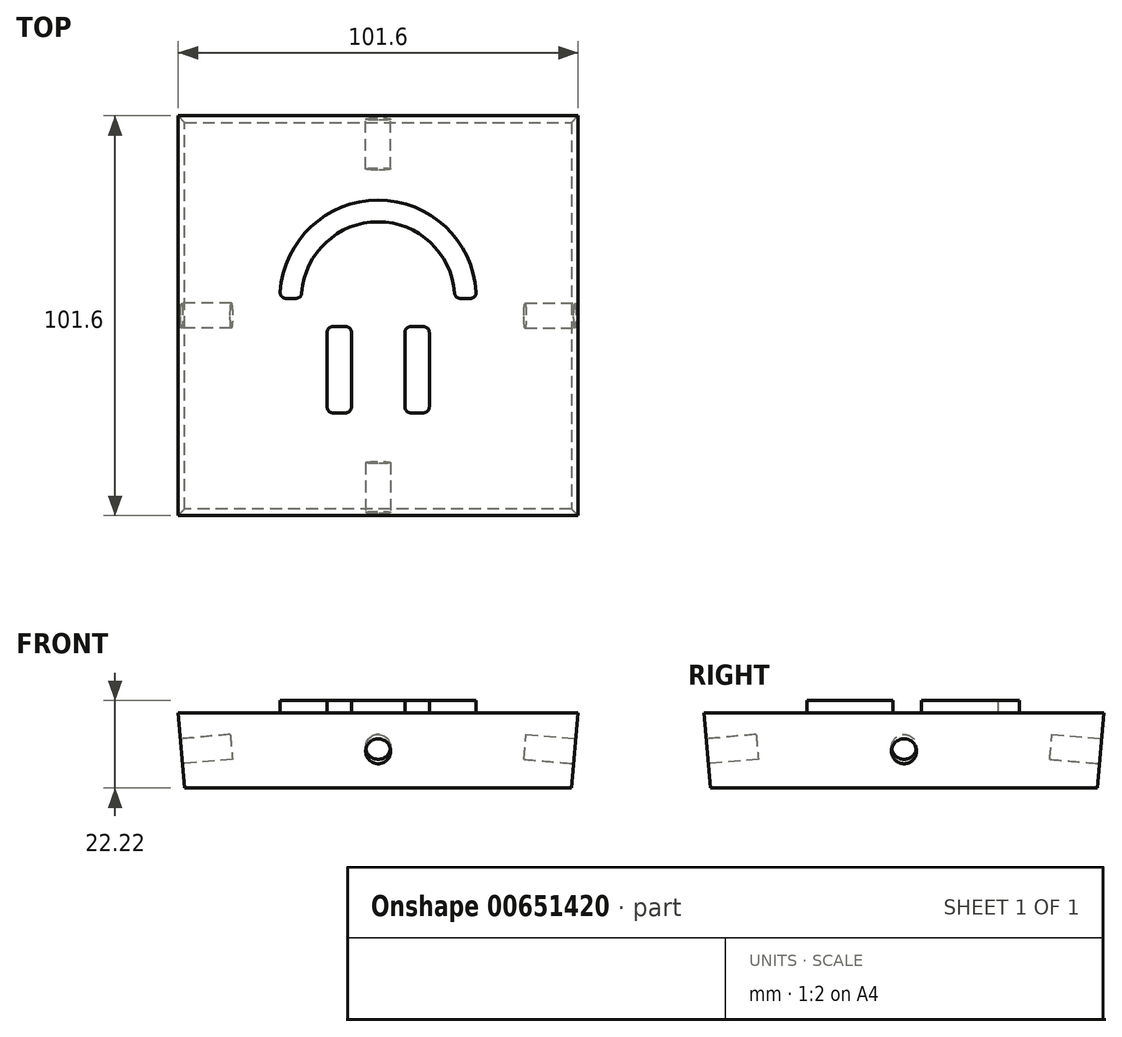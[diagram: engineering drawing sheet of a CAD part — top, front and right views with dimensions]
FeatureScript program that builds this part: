
annotation { "Feature Type Name" : "Feature", "Feature Type Description" : "" }
export const myFeature = defineFeature(function(context is Context, id is Id, definition is map)
    precondition{}
    {
        {
            var Q0;
            Q0=qCreatedBy(makeId("Top.planeOp"),FACE);
            var sketch = newSketch(context, id + "F0", { "sketchPlane" : qUnion([Q0])});
            skLineSegment(sketch, "E0.bottom", {"start": v(-50.8, 50.8) * mm, "end": v(50.8, 50.8) * mm});
            skLineSegment(sketch, "E0.top", {"start": v(-50.8, -50.8) * mm, "end": v(50.8, -50.8) * mm});
            skLineSegment(sketch, "E0.left", {"start": v(-50.8, 50.8) * mm, "end": v(-50.8, -50.8) * mm});
            skLineSegment(sketch, "E0.right", {"start": v(50.8, 50.8) * mm, "end": v(50.8, -50.8) * mm});
            skPoint(sketch, "E0.middle", {"position": v(0, 0) * mm});
            skSolve(sketch);
        }
        {
            var Q0;
            Q0=makeQuery(id+"F0.imprint","IMPRINT",FACE,{"disambiguationData":[TD([[makeQuery(id+"F0.imprint","IMPRINT",EDGE,{"derivedFrom":sQuery(id+"F0.wireOp",EDGE,"E0.bottom")}),-1.0]])]});
            extrude(context, id + "F1", {"entities" : qUnion([Q0]), "depth" : 19.05 * mm, "offsetDistance" : 25.4 * mm});
        }
        {
            var Q0;
            Q0=makeQuery(id+"F1.opExtrude","CAP_EDGE",EDGE,{"disambiguationData":[OSD([sQuery(id+"F0.wireOp",EDGE,"E0.right")])],"isStart":false});
            var Q1;
            Q1=makeQuery(id+"F1.opExtrude","CAP_EDGE",EDGE,{"disambiguationData":[OSD([sQuery(id+"F0.wireOp",EDGE,"E0.top")])],"isStart":false});
            var Q2;
            Q2=makeQuery(id+"F1.opExtrude","CAP_EDGE",EDGE,{"disambiguationData":[OSD([sQuery(id+"F0.wireOp",EDGE,"E0.left")])],"isStart":false});
            var Q3;
            Q3=makeQuery(id+"F1.opExtrude","CAP_EDGE",EDGE,{"disambiguationData":[OSD([sQuery(id+"F0.wireOp",EDGE,"E0.bottom")])],"isStart":false});
            chamfer(context, id + "F2", {"entities" : qUnion([Q0, Q1, Q2, Q3]), "chamferType" : ChamferType.OFFSET_ANGLE, "width" : 19.05 * mm, "oppositeDirection" : false, "angle" : 5 * degree, "tangentPropagation" : true});
        }
        {
            var Q0;
            Q0=makeQuery(id+"F2.opChamfer","BLEND_FACE",FACE,{"disambiguationData":[OSD([sQuery(id+"F0.wireOp",EDGE,"E0.bottom")])]});
            var sketch = newSketch(context, id + "F3", { "sketchPlane" : qUnion([Q0])});
            skLineSegment(sketch, "E1", {"start": v(-49.13, 14.7) * mm, "end": v(50.8, -4.43) * mm, "construction": true});
            skLineSegment(sketch, "E2", {"start": v(-50.8, -4.43) * mm, "end": v(49.13, 14.7) * mm, "construction": true});
            skCircle(sketch, "E3", {"center": v(0, 5.3) * mm, "radius": 3.18 * mm});
            skSolve(sketch);
        }
        {
            var Q0;
            Q0=makeQuery(id+"F3.imprint","IMPRINT",FACE,{"disambiguationData":[TD([[makeQuery(id+"F3.imprint","IMPRINT",EDGE,{"derivedFrom":sQuery(id+"F3.wireOp",EDGE,"E3")}),1.0]])]});
            extrude(context, id + "F4", {"entities" : qUnion([Q0]), "operationType" : NewBodyOperationType.REMOVE, "oppositeDirection" : true, "depth" : 12.7 * mm, "offsetDistance" : 25.4 * mm});
        }
        {
            var Q0;
            Q0=makeQuery(id+"F2.opChamfer","BLEND_FACE",FACE,{"disambiguationData":[OSD([sQuery(id+"F0.wireOp",EDGE,"E0.left")])]});
            var sketch = newSketch(context, id + "F5", { "sketchPlane" : qUnion([Q0])});
            skLineSegment(sketch, "E4", {"start": v(-49.13, 14.7) * mm, "end": v(50.8, -4.43) * mm, "construction": true});
            skLineSegment(sketch, "E5", {"start": v(-50.8, -4.43) * mm, "end": v(49.13, 14.7) * mm, "construction": true});
            skCircle(sketch, "E6", {"center": v(0, 5.3) * mm, "radius": 3.18 * mm});
            skSolve(sketch);
        }
        {
            var Q0;
            Q0=makeQuery(id+"F2.opChamfer","BLEND_FACE",FACE,{"disambiguationData":[OSD([sQuery(id+"F0.wireOp",EDGE,"E0.top")])]});
            var sketch = newSketch(context, id + "F6", { "sketchPlane" : qUnion([Q0])});
            skLineSegment(sketch, "E7", {"start": v(-49.13, 14.7) * mm, "end": v(50.8, -4.43) * mm, "construction": true});
            skLineSegment(sketch, "E8", {"start": v(-50.8, -4.43) * mm, "end": v(49.13, 14.7) * mm, "construction": true});
            skCircle(sketch, "E9", {"center": v(0, 5.3) * mm, "radius": 3.18 * mm});
            skSolve(sketch);
        }
        {
            var Q0;
            Q0=makeQuery(id+"F2.opChamfer","BLEND_FACE",FACE,{"disambiguationData":[OSD([sQuery(id+"F0.wireOp",EDGE,"E0.right")])]});
            var sketch = newSketch(context, id + "F7", { "sketchPlane" : qUnion([Q0])});
            skLineSegment(sketch, "E10", {"start": v(-49.13, 14.7) * mm, "end": v(50.8, -4.43) * mm, "construction": true});
            skLineSegment(sketch, "E11", {"start": v(-50.8, -4.43) * mm, "end": v(49.13, 14.7) * mm, "construction": true});
            skCircle(sketch, "E12", {"center": v(0, 5.3) * mm, "radius": 3.18 * mm});
            skSolve(sketch);
        }
        {
            var Q0;
            Q0=makeQuery(id+"F7.imprint","IMPRINT",FACE,{"disambiguationData":[TD([[makeQuery(id+"F7.imprint","IMPRINT",EDGE,{"derivedFrom":sQuery(id+"F7.wireOp",EDGE,"E12")}),1.0]])]});
            extrude(context, id + "F8", {"entities" : qUnion([Q0]), "operationType" : NewBodyOperationType.REMOVE, "oppositeDirection" : true, "depth" : 12.7 * mm, "offsetDistance" : 25.4 * mm});
        }
        {
            var Q0;
            Q0=makeQuery(id+"F6.imprint","IMPRINT",FACE,{"disambiguationData":[TD([[makeQuery(id+"F6.imprint","IMPRINT",EDGE,{"derivedFrom":sQuery(id+"F6.wireOp",EDGE,"E9")}),1.0]])]});
            extrude(context, id + "F9", {"entities" : qUnion([Q0]), "operationType" : NewBodyOperationType.REMOVE, "oppositeDirection" : true, "depth" : 12.7 * mm, "offsetDistance" : 25.4 * mm});
        }
        {
            var Q0;
            Q0=makeQuery(id+"F5.imprint","IMPRINT",FACE,{"disambiguationData":[TD([[makeQuery(id+"F5.imprint","IMPRINT",EDGE,{"derivedFrom":sQuery(id+"F5.wireOp",EDGE,"E6")}),1.0]])]});
            extrude(context, id + "F10", {"entities" : qUnion([Q0]), "operationType" : NewBodyOperationType.REMOVE, "oppositeDirection" : true, "depth" : 12.7 * mm, "offsetDistance" : 25.4 * mm});
        }
        {
            var Q0;
            Q0=makeQuery(id+"F1.opExtrude","CAP_FACE",FACE,{"disambiguationData":[OSD([sQuery(id+"F0.wireOp",EDGE,"E0.bottom"),sQuery(id+"F0.wireOp",EDGE,"E0.top"),sQuery(id+"F0.wireOp",EDGE,"E0.left"),sQuery(id+"F0.wireOp",EDGE,"E0.right")])],"isStart":true});
            var sketch = newSketch(context, id + "F11", { "sketchPlane" : qUnion([Q0])});
            skLineSegment(sketch, "E13.bottom", {"start": v(-11.51, 24.67) * mm, "end": v(-8.25, 24.67) * mm});
            skLineSegment(sketch, "E13.top", {"start": v(-11.51, 2.78) * mm, "end": v(-8.25, 2.78) * mm});
            skLineSegment(sketch, "E13.left", {"start": v(-12.99, 23.2) * mm, "end": v(-12.99, 4.25) * mm});
            skLineSegment(sketch, "E13.right", {"start": v(-6.78, 23.2) * mm, "end": v(-6.78, 4.25) * mm});
            skLineSegment(sketch, "E14", {"start": v(0, 0) * mm, "end": v(0, 24.5) * mm, "construction": true});
            skLineSegment(sketch, "E15.MirrorCS", {"start": v(11.51, 24.67) * mm, "end": v(8.25, 24.67) * mm});
            skLineSegment(sketch, "E16.MirrorCS", {"start": v(11.51, 2.78) * mm, "end": v(8.25, 2.78) * mm});
            skLineSegment(sketch, "E17.MirrorCS", {"start": v(6.78, 23.2) * mm, "end": v(6.78, 4.25) * mm});
            skLineSegment(sketch, "E18.MirrorCS", {"start": v(12.99, 23.2) * mm, "end": v(12.99, 4.25) * mm});
            skArc(sketch, "E19", {"start": v(-19.4, -5.78) * mm, "mid": v(0, -23.86) * mm, "end": v(19.4, -5.78) * mm});
            skArc(sketch, "E20", {"start": v(-24.9, -5.97) * mm, "mid": v(0, -29.36) * mm, "end": v(24.9, -5.97) * mm});
            skLineSegment(sketch, "E21", {"start": v(-23.43, -4.4) * mm, "end": v(-20.87, -4.4) * mm});
            skLineSegment(sketch, "E22.trimOffspring", {"start": v(20.87, -4.4) * mm, "end": v(23.43, -4.4) * mm});
            skPoint(sketch, "E23.visualSharp", {"position": v(-24.95, -4.4) * mm});
            skArc(sketch, "E23.filletArc", {"start": v(-23.43, -4.4) * mm, "mid": v(-24.5, -4.87) * mm, "end": v(-24.9, -5.97) * mm});
            skPoint(sketch, "E24.visualSharp", {"position": v(19.45, -4.4) * mm});
            skArc(sketch, "E24.filletArc", {"start": v(20.87, -4.4) * mm, "mid": v(19.86, -4.8) * mm, "end": v(19.4, -5.78) * mm});
            skPoint(sketch, "E25.visualSharp", {"position": v(-19.45, -4.4) * mm});
            skArc(sketch, "E25.filletArc", {"start": v(-19.4, -5.78) * mm, "mid": v(-19.86, -4.8) * mm, "end": v(-20.87, -4.4) * mm});
            skPoint(sketch, "E26.visualSharp", {"position": v(24.95, -4.4) * mm});
            skArc(sketch, "E26.filletArc", {"start": v(24.9, -5.97) * mm, "mid": v(24.5, -4.87) * mm, "end": v(23.43, -4.4) * mm});
            skPoint(sketch, "E27.visualSharp", {"position": v(6.78, 24.67) * mm});
            skArc(sketch, "E27.filletArc", {"start": v(8.25, 24.67) * mm, "mid": v(7.21, 24.24) * mm, "end": v(6.78, 23.2) * mm});
            skPoint(sketch, "E28.visualSharp", {"position": v(12.99, 24.67) * mm});
            skArc(sketch, "E28.filletArc", {"start": v(12.99, 23.2) * mm, "mid": v(12.56, 24.24) * mm, "end": v(11.51, 24.67) * mm});
            skPoint(sketch, "E29.visualSharp", {"position": v(6.78, 2.78) * mm});
            skArc(sketch, "E29.filletArc", {"start": v(6.78, 4.25) * mm, "mid": v(7.21, 3.2) * mm, "end": v(8.25, 2.78) * mm});
            skPoint(sketch, "E30.visualSharp", {"position": v(12.99, 2.78) * mm});
            skArc(sketch, "E30.filletArc", {"start": v(11.51, 2.78) * mm, "mid": v(12.56, 3.2) * mm, "end": v(12.99, 4.25) * mm});
            skPoint(sketch, "E31.visualSharp", {"position": v(-12.99, 24.67) * mm});
            skArc(sketch, "E31.filletArc", {"start": v(-11.51, 24.67) * mm, "mid": v(-12.56, 24.24) * mm, "end": v(-12.99, 23.2) * mm});
            skPoint(sketch, "E32.visualSharp", {"position": v(-6.78, 24.67) * mm});
            skArc(sketch, "E32.filletArc", {"start": v(-6.78, 23.2) * mm, "mid": v(-7.21, 24.24) * mm, "end": v(-8.25, 24.67) * mm});
            skPoint(sketch, "E33.visualSharp", {"position": v(-12.99, 2.78) * mm});
            skArc(sketch, "E33.filletArc", {"start": v(-12.99, 4.25) * mm, "mid": v(-12.56, 3.2) * mm, "end": v(-11.51, 2.78) * mm});
            skPoint(sketch, "E34.visualSharp", {"position": v(-6.78, 2.78) * mm});
            skArc(sketch, "E34.filletArc", {"start": v(-8.25, 2.78) * mm, "mid": v(-7.21, 3.2) * mm, "end": v(-6.78, 4.25) * mm});
            skSolve(sketch);
        }
        {
            var Q0;
            Q0=qSketchRegion(id+"F11",true);
            extrude(context, id + "F12", {"entities" : qUnion([Q0]), "operationType" : NewBodyOperationType.ADD, "depth" : 3.17 * mm, "offsetDistance" : 25.4 * mm});
        }
        {
            var Q0;
            Q0=makeQuery(id+"F1.opExtrude","CAP_FACE",FACE,{"disambiguationData":[OSD([sQuery(id+"F0.wireOp",EDGE,"E0.bottom"),sQuery(id+"F0.wireOp",EDGE,"E0.top"),sQuery(id+"F0.wireOp",EDGE,"E0.left"),sQuery(id+"F0.wireOp",EDGE,"E0.right")])],"isStart":false});
            var sketch = newSketch(context, id + "F13", { "sketchPlane" : qUnion([Q0])});
            skLineSegment(sketch, "E35", {"start": v(55.15, 29.48) * mm, "end": v(55.15, -28.93) * mm, "construction": true});
            skSolve(sketch);
        }
        {
            var Q0;
            Q0=makeQuery(id+"F1.opExtrude","SWEPT_BODY",BODY,{"disambiguationData":[OSD([sQuery(id+"F0.wireOp",EDGE,"E0.bottom"),sQuery(id+"F0.wireOp",EDGE,"E0.top"),sQuery(id+"F0.wireOp",EDGE,"E0.left"),sQuery(id+"F0.wireOp",EDGE,"E0.right")])]});
            var Q1;
            Q1=sQuery(id+"F13.wireOp",EDGE,"E35");
            transform(context, id + "F14", {"entities" : qUnion([Q0]), "transformType" : TransformType.ROTATION, "transformAxis" : qUnion([Q1]), "angle" : 180 * degree, "makeCopy" : false});
        }
    });
